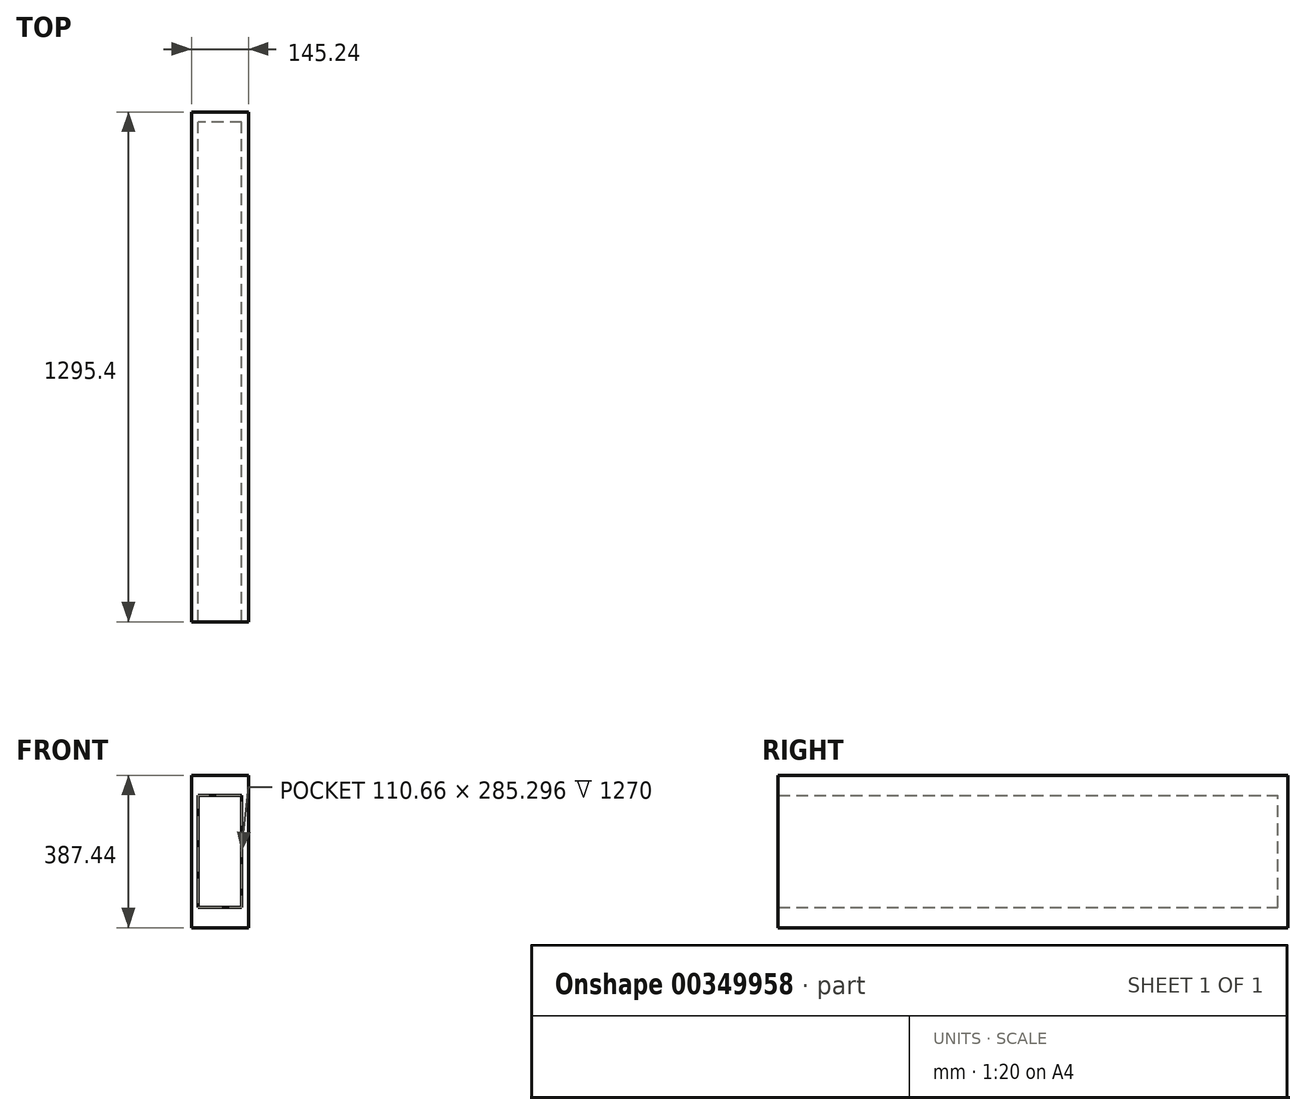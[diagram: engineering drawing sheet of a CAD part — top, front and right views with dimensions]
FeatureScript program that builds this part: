
annotation { "Feature Type Name" : "Feature", "Feature Type Description" : "" }
export const myFeature = defineFeature(function(context is Context, id is Id, definition is map)
    precondition{}
    {
        {
            var Q0;
            Q0=qCreatedBy(makeId("Front.planeOp"),FACE);
            var sketch = newSketch(context, id + "F0", { "sketchPlane" : qUnion([Q0])});
            skLineSegment(sketch, "E0.bottom", {"start": v(72.62, -193.72) * mm, "end": v(-72.62, -193.72) * mm});
            skLineSegment(sketch, "E0.top", {"start": v(72.62, 193.72) * mm, "end": v(-72.62, 193.72) * mm});
            skLineSegment(sketch, "E0.left", {"start": v(72.62, -193.72) * mm, "end": v(72.62, 193.72) * mm});
            skLineSegment(sketch, "E0.right", {"start": v(-72.62, -193.72) * mm, "end": v(-72.62, 193.72) * mm});
            skPoint(sketch, "E0.middle", {"position": v(0, 0) * mm});
            skLineSegment(sketch, "E1.bottom", {"start": v(55.33, -142.65) * mm, "end": v(-55.33, -142.65) * mm});
            skLineSegment(sketch, "E1.top", {"start": v(55.33, 142.65) * mm, "end": v(-55.33, 142.65) * mm});
            skLineSegment(sketch, "E1.left", {"start": v(55.33, -142.65) * mm, "end": v(55.33, 142.65) * mm});
            skLineSegment(sketch, "E1.right", {"start": v(-55.33, -142.65) * mm, "end": v(-55.33, 142.65) * mm});
            skSolve(sketch);
        }
        {
            var Q0;
            Q0 = qSketchRegion(id + "F0", true);
            extrude(context, id + "F1", {"entities" : qUnion([Q0]), "depth" : 1270 * mm});
        }
        {
            var Q0;
            Q0=makeQuery(id+"F1.opExtrude","CAP_FACE",FACE,{"disambiguationData":[OSD([sQuery(id+"F0.wireOp",EDGE,"E0.bottom"),sQuery(id+"F0.wireOp",EDGE,"E0.top"),sQuery(id+"F0.wireOp",EDGE,"E0.left"),sQuery(id+"F0.wireOp",EDGE,"E0.right"),sQuery(id+"F0.wireOp",EDGE,"E1.bottom"),sQuery(id+"F0.wireOp",EDGE,"E1.top"),sQuery(id+"F0.wireOp",EDGE,"E1.left"),sQuery(id+"F0.wireOp",EDGE,"E1.right")])],"isStart":true});
            var sketch = newSketch(context, id + "F2", { "sketchPlane" : qUnion([Q0])});
            skLineSegment(sketch, "E2.bottom", {"start": v(72.62, -193.72) * mm, "end": v(-72.62, -193.72) * mm});
            skLineSegment(sketch, "E2.top", {"start": v(72.62, 193.72) * mm, "end": v(-72.62, 193.72) * mm});
            skLineSegment(sketch, "E2.left", {"start": v(72.62, -193.72) * mm, "end": v(72.62, 193.72) * mm});
            skLineSegment(sketch, "E2.right", {"start": v(-72.62, -193.72) * mm, "end": v(-72.62, 193.72) * mm});
            skPoint(sketch, "E2.middle", {"position": v(0, 0) * mm});
            skSolve(sketch);
        }
        {
            var Q0;
            Q0 = qSketchRegion(id + "F2", true);
            extrude(context, id + "F3", {"entities" : qUnion([Q0]), "operationType" : NewBodyOperationType.ADD, "depth" : 25.4 * mm});
        }
    });
